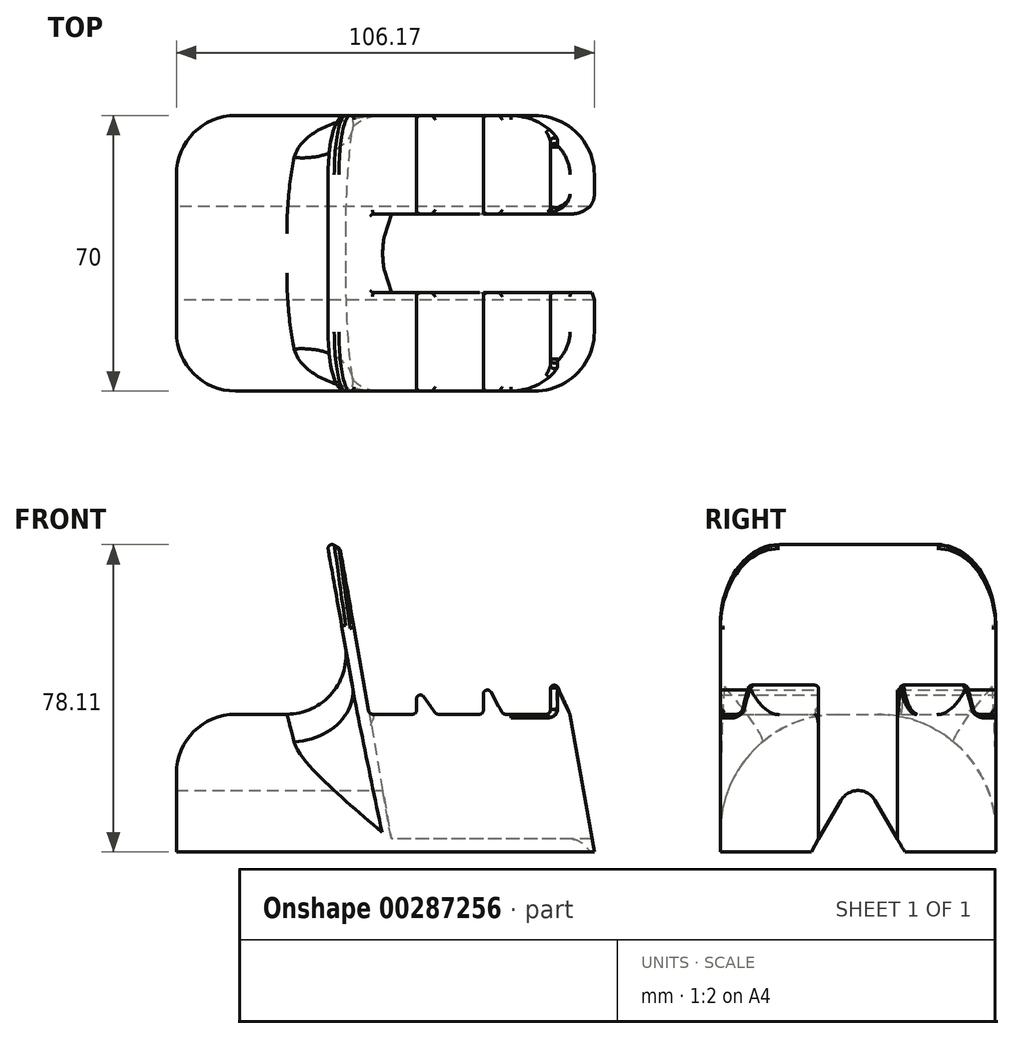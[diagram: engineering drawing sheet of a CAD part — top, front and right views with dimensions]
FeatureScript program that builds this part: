
annotation { "Feature Type Name" : "Feature", "Feature Type Description" : "" }
export const myFeature = defineFeature(function(context is Context, id is Id, definition is map)
    precondition{}
    {
        {
            var Q0;
            Q0=qCreatedBy(makeId("Front.planeOp"),FACE);
            var sketch = newSketch(context, id + "F0", { "sketchPlane" : qUnion([Q0])});
            skLineSegment(sketch, "E0.bottom", {"start": v(-55.17, 35) * mm, "end": v(-9.22, 35) * mm});
            skLineSegment(sketch, "E0.top", {"start": v(-55.17, 0) * mm, "end": v(51, 0) * mm});
            skLineSegment(sketch, "E0.left", {"start": v(-55.17, 35) * mm, "end": v(-55.17, 0) * mm});
            skLineSegment(sketch, "E0.right", {"start": v(44.83, 35) * mm, "end": v(51, 0) * mm});
            skLineSegment(sketch, "E1", {"start": v(-6.17, 35) * mm, "end": v(-13.56, 76.88) * mm});
            skLineSegment(sketch, "E2", {"start": v(-17.03, 79.32) * mm, "end": v(-9.22, 35) * mm});
            skLineSegment(sketch, "E3.top", {"start": v(5.83, 42) * mm, "end": v(11.13, 42) * mm});
            skLineSegment(sketch, "E3.left", {"start": v(5.83, 35) * mm, "end": v(5.83, 42) * mm});
            skLineSegment(sketch, "E4.top", {"start": v(22.83, 44) * mm, "end": v(28.12, 44) * mm});
            skLineSegment(sketch, "E4.left", {"start": v(22.83, 35) * mm, "end": v(22.83, 44) * mm});
            skLineSegment(sketch, "E4.right", {"start": v(27.83, 35) * mm, "end": v(27.83, 35) * mm});
            skLineSegment(sketch, "E5.right", {"start": v(39.83, 35) * mm, "end": v(39.83, 46) * mm});
            skLineSegment(sketch, "E6.trimOffspring", {"start": v(-6.17, 35) * mm, "end": v(5.83, 35) * mm});
            skPoint(sketch, "E7.orphan", {"position": v(0, 0) * mm});
            skLineSegment(sketch, "E8.trimOffspring", {"start": v(10.83, 35) * mm, "end": v(22.83, 35) * mm});
            skLineSegment(sketch, "E9.trimOffspring", {"start": v(27.83, 35) * mm, "end": v(39.83, 35) * mm});
            skLineSegment(sketch, "E10", {"start": v(5.83, 42) * mm, "end": v(10.83, 35) * mm});
            skLineSegment(sketch, "E11", {"start": v(22.83, 44) * mm, "end": v(27.83, 35) * mm});
            skLineSegment(sketch, "E12", {"start": v(39.83, 46) * mm, "end": v(44.83, 35) * mm});
            skLineSegment(sketch, "E13", {"start": v(-17.03, 79.32) * mm, "end": v(-13.56, 76.88) * mm});
            skSolve(sketch);
        }
        {
            var Q0;
            Q0=makeQuery(id+"F0.imprint","IMPRINT",FACE,{"disambiguationData":[TD([[makeQuery(id+"F0.imprint","IMPRINT",EDGE,{"derivedFrom":sQuery(id+"F0.wireOp",EDGE,"E0.bottom")}),-1.0]])]});
            extrude(context, id + "F1", {"entities" : qUnion([Q0]), "endBound" : BoundingType.SYMMETRIC, "depth" : 70 * mm});
        }
        {
            var Q0;
            Q0=makeQuery(id+"F1.opExtrude","SWEPT_FACE",FACE,{"disambiguationData":[OSD([sQuery(id+"F0.wireOp",EDGE,"E0.right")])]});
            var sketch = newSketch(context, id + "F2", { "sketchPlane" : qUnion([Q0])});
            skLineSegment(sketch, "E14.bottom", {"start": v(-10, 40.35) * mm, "end": v(10, 40.35) * mm});
            skLineSegment(sketch, "E14.left", {"start": v(-10, 40.35) * mm, "end": v(-10, -8.86) * mm});
            skLineSegment(sketch, "E14.right", {"start": v(10, 40.35) * mm, "end": v(10, -8.86) * mm});
            skPoint(sketch, "E14.middle", {"position": v(0, -8.86) * mm});
            skLineSegment(sketch, "E15", {"start": v(-10, -8.86) * mm, "end": v(10, -8.86) * mm});
            skSolve(sketch);
        }
        {
            var Q0;
            Q0=qSketchRegion(id+"F2",true);
            var Q1;
            Q1=makeQuery(id+"F1.opExtrude","SWEPT_FACE",FACE,{"disambiguationData":[OSD([sQuery(id+"F0.wireOp",EDGE,"E1")])]});
            extrude(context, id + "F3", {"entities" : qUnion([Q0]), "operationType" : NewBodyOperationType.REMOVE, "endBound" : BoundingType.UP_TO_SURFACE, "oppositeDirection" : true, "endBoundEntityFace" : qUnion([Q1]), "depth" : 25 * mm});
        }
        {
            var Q0;
            Q0=makeQuery(id+"F1.opExtrude","SWEPT_FACE",FACE,{"disambiguationData":[OSD([sQuery(id+"F0.wireOp",EDGE,"E0.left")])]});
            var sketch = newSketch(context, id + "F4", { "sketchPlane" : qUnion([Q0])});
            skLineSegment(sketch, "E16", {"start": v(0, 0) * mm, "end": v(11.9, 0) * mm});
            skLineSegment(sketch, "E17", {"start": v(11.9, 0) * mm, "end": v(0, 20.6) * mm});
            skLineSegment(sketch, "E18", {"start": v(0, 20.6) * mm, "end": v(-11.9, 0) * mm});
            skLineSegment(sketch, "E19", {"start": v(-11.9, 0) * mm, "end": v(0, 0) * mm});
            skSolve(sketch);
        }
        {
            var Q0;
            Q0=makeQuery(id+"F4.imprint","IMPRINT",FACE,{"disambiguationData":[TD([[makeQuery(id+"F4.imprint","IMPRINT",EDGE,{"derivedFrom":sQuery(id+"F4.wireOp",EDGE,"E16")}),-1.0]])]});
            extrude(context, id + "F5", {"entities" : qUnion([Q0]), "operationType" : NewBodyOperationType.REMOVE, "endBound" : BoundingType.THROUGH_ALL, "oppositeDirection" : true, "depth" : 25 * mm});
        }
        {
            var Q0;
            Q0=makeQuery(id+"F1.opExtrude","CAP_EDGE",EDGE,{"disambiguationData":[OSD([sQuery(id+"F0.wireOp",EDGE,"E13")])],"isStart":false});
            var Q1;
            Q1=makeQuery(id+"F1.opExtrude","CAP_EDGE",EDGE,{"disambiguationData":[OSD([sQuery(id+"F0.wireOp",EDGE,"E13")])],"isStart":true});
            fillet(context, id + "F6", {"entities" : qUnion([Q0, Q1]), "radius" : 15 * mm, "tangentPropagation" : true, "allowEdgeOverflow" : false});
        }
        {
            var Q0;
            Q0=makeQuery(id+"F5.boolean.opBoolean","COPY",EDGE,{"derivedFrom":makeQuery(id+"F5.opExtrude","SWEPT_EDGE",EDGE,{"disambiguationData":[OSD([sQuery(id+"F4.wireOp",EDGE,"E17"),sQuery(id+"F4.wireOp",EDGE,"E18")])]})});
            fillet(context, id + "F7", {"entities" : qUnion([Q0]), "radius" : 5 * mm, "tangentPropagation" : true, "allowEdgeOverflow" : false});
        }
        {
            var Q0;
            Q0=makeQuery(id+"F1.opExtrude","CAP_EDGE",EDGE,{"disambiguationData":[OSD([sQuery(id+"F0.wireOp",EDGE,"E0.right")])],"isStart":false});
            var Q1;
            Q1=makeQuery(id+"F1.opExtrude","CAP_EDGE",EDGE,{"disambiguationData":[OSD([sQuery(id+"F0.wireOp",EDGE,"E0.right")])],"isStart":true});
            fillet(context, id + "F8", {"entities" : qUnion([Q0, Q1]), "radius" : 15 * mm, "tangentPropagation" : true, "allowEdgeOverflow" : false});
        }
        {
            var Q0;
            Q0=makeQuery(id+"F3.boolean.opBoolean","COPY",EDGE,{"derivedFrom":makeQuery(id+"F3.opExtrude","CAP_EDGE",EDGE,{"disambiguationData":[OSD([sQuery(id+"F2.wireOp",EDGE,"E14.left")])],"isStart":true})});
            var Q1;
            Q1=makeQuery(id+"F3.boolean.opBoolean","COPY",EDGE,{"derivedFrom":makeQuery(id+"F3.opExtrude","CAP_EDGE",EDGE,{"disambiguationData":[OSD([sQuery(id+"F2.wireOp",EDGE,"E14.right")])],"isStart":true})});
            fillet(context, id + "F9", {"entities" : qUnion([Q0, Q1]), "radius" : 5 * mm, "tangentPropagation" : true, "allowEdgeOverflow" : false});
        }
        {
            var Q0;
            {var subQ2=sQuery(id+"F0.wireOp",EDGE,"E6.trimOffspring");Q0=makeQuery(id+"F3.boolean.opBoolean","SPLIT",FACE,{"disambiguationData":[TD([makeQuery(id+"F3.opExtrude","SWEPT_FACE",FACE,{"disambiguationData":[OSD([sQuery(id+"F2.wireOp",EDGE,"E14.left")])]})])],"derivedFrom":makeQuery(id+"F1.opExtrude","SWEPT_FACE",FACE,{"disambiguationData":[OSD([subQ2])]})});}
            var Q1;
            {var subQ1=sQuery(id+"F0.wireOp",EDGE,"E8.trimOffspring");Q1=makeQuery(id+"F3.boolean.opBoolean","SPLIT",FACE,{"disambiguationData":[TD([makeQuery(id+"F3.opExtrude","SWEPT_FACE",FACE,{"disambiguationData":[OSD([sQuery(id+"F2.wireOp",EDGE,"E14.left")])]})])],"derivedFrom":makeQuery(id+"F1.opExtrude","SWEPT_FACE",FACE,{"disambiguationData":[OSD([subQ1])]})});}
            var Q2;
            {var subQ1=sQuery(id+"F0.wireOp",EDGE,"E6.trimOffspring");Q2=makeQuery(id+"F3.boolean.opBoolean","SPLIT",FACE,{"disambiguationData":[TD([makeQuery(id+"F3.opExtrude","SWEPT_FACE",FACE,{"disambiguationData":[OSD([sQuery(id+"F2.wireOp",EDGE,"E14.right")])]})])],"derivedFrom":makeQuery(id+"F1.opExtrude","SWEPT_FACE",FACE,{"disambiguationData":[OSD([subQ1])]})});}
            var Q3;
            {var subQ1=sQuery(id+"F0.wireOp",EDGE,"E8.trimOffspring");Q3=makeQuery(id+"F3.boolean.opBoolean","SPLIT",FACE,{"disambiguationData":[TD([makeQuery(id+"F3.opExtrude","SWEPT_FACE",FACE,{"disambiguationData":[OSD([sQuery(id+"F2.wireOp",EDGE,"E14.right")])]})])],"derivedFrom":makeQuery(id+"F1.opExtrude","SWEPT_FACE",FACE,{"disambiguationData":[OSD([subQ1])]})});}
            fillet(context, id + "F10", {"entities" : qUnion([Q0, Q1, Q2, Q3]), "radius" : 1 * mm, "tangentPropagation" : true, "allowEdgeOverflow" : false});
        }
        {
            var Q0;
            Q0=makeQuery(id+"F1.opExtrude","SWEPT_EDGE",EDGE,{"disambiguationData":[OSD([sQuery(id+"F0.wireOp",EDGE,"E3.left"),sQuery(id+"F0.wireOp",EDGE,"8321fb7f-3458-440f-b528-b5414c48c93d.filletArc")])]});
            var Q1;
            Q1=makeQuery(id+"F1.opExtrude","SWEPT_EDGE",EDGE,{"disambiguationData":[OSD([sQuery(id+"F0.wireOp",EDGE,"E4.left"),sQuery(id+"F0.wireOp",EDGE,"d95e2400-caf3-4430-b733-34f4ab988b37.filletArc")])]});
            var Q2;
            Q2=makeQuery(id+"F1.opExtrude","SWEPT_EDGE",EDGE,{"disambiguationData":[OSD([sQuery(id+"F0.wireOp",EDGE,"E5.right"),sQuery(id+"F0.wireOp",EDGE,"e5e4de03-1c67-4efd-834d-6cea7254acc7.filletArc")])]});
            fillet(context, id + "F11", {"entities" : qUnion([Q0, Q1, Q2]), "radius" : 1 * mm, "tangentPropagation" : true, "allowEdgeOverflow" : false});
        }
        {
            var Q0;
            Q0=makeQuery(id+"F1.opExtrude","SWEPT_EDGE",EDGE,{"disambiguationData":[OSD([sQuery(id+"F0.wireOp",EDGE,"E1"),sQuery(id+"F0.wireOp",EDGE,"E13")])]});
            fillet(context, id + "F12", {"entities" : qUnion([Q0]), "radius" : 1 * mm, "tangentPropagation" : true, "allowEdgeOverflow" : false});
        }
        {
            var Q0;
            Q0=makeQuery(id+"F1.opExtrude","CAP_EDGE",EDGE,{"disambiguationData":[OSD([sQuery(id+"F0.wireOp",EDGE,"E0.bottom")])],"isStart":true});
            var Q1;
            Q1=makeQuery(id+"F1.opExtrude","CAP_EDGE",EDGE,{"disambiguationData":[OSD([sQuery(id+"F0.wireOp",EDGE,"E0.bottom")])],"isStart":false});
            fillet(context, id + "F13", {"entities" : qUnion([Q0, Q1]), "radius" : 30 * mm, "tangentPropagation" : true, "allowEdgeOverflow" : false});
        }
        {
            var Q0;
            Q0=makeQuery(id+"F1.opExtrude","CAP_EDGE",EDGE,{"disambiguationData":[OSD([sQuery(id+"F0.wireOp",EDGE,"E2")])],"isStart":true});
            fillet(context, id + "F14", {"entities" : qUnion([Q0]), "radius" : 1 * mm, "tangentPropagation" : true, "allowEdgeOverflow" : false});
        }
        {
            var Q0;
            {var subQ0=sQuery(id+"F0.wireOp",EDGE,"E0.bottom");Q0=makeQuery(id+"F13.opFillet","BLEND_FACE",FACE,{"disambiguationData":[OSD([subQ0]),TDD([makeQuery(id+"F1.opExtrude","CAP_EDGE",EDGE,{"disambiguationData":[OSD([subQ0])],"isStart":true})])]});}
            fillet(context, id + "F15", {"entities" : qUnion([Q0]), "radius" : 15 * mm, "tangentPropagation" : true, "allowEdgeOverflow" : false});
        }
        {
            var Q0;
            {var subQ1=sQuery(id+"F0.wireOp",EDGE,"E9.trimOffspring");Q0=makeQuery(id+"F3.boolean.opBoolean","SPLIT",FACE,{"disambiguationData":[TD([makeQuery(id+"F3.opExtrude","SWEPT_FACE",FACE,{"disambiguationData":[OSD([sQuery(id+"F2.wireOp",EDGE,"E14.left")])]})])],"derivedFrom":makeQuery(id+"F1.opExtrude","SWEPT_FACE",FACE,{"disambiguationData":[OSD([subQ1])]})});}
            var Q1;
            {var subQ1=sQuery(id+"F0.wireOp",EDGE,"E9.trimOffspring");Q1=makeQuery(id+"F3.boolean.opBoolean","SPLIT",FACE,{"disambiguationData":[TD([makeQuery(id+"F3.opExtrude","SWEPT_FACE",FACE,{"disambiguationData":[OSD([sQuery(id+"F2.wireOp",EDGE,"E14.right")])]})])],"derivedFrom":makeQuery(id+"F1.opExtrude","SWEPT_FACE",FACE,{"disambiguationData":[OSD([subQ1])]})});}
            fillet(context, id + "F16", {"entities" : qUnion([Q0, Q1]), "radius" : 1 * mm, "tangentPropagation" : true, "allowEdgeOverflow" : false});
        }
    });
